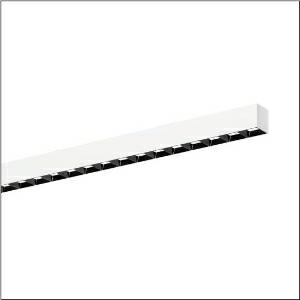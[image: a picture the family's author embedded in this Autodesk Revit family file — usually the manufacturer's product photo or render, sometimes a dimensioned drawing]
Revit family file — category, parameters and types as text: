
# Revit family: silica_21_51mx24tat4w
name_source: partatom
category: Lighting Fixtures
units: mm (PartAtom-declared; Revit-internal decimal feet)

## family parameters
Cut with Voids When Loaded = No
Host = Face
Light Source = No
Part Type = Normal
Room Calculation Point = No
Round Connector Dimension = Use Diameter
Shared = No

## types (1)
- --- (1 x LED, 3280 lm, 32.4 W, 6500K)
    Apparent Load = 32 VA
    CIE Flux Codes = 74 94 99 100 100
    Color Rendering = 80
    Color Temperature = 6500K
    Default Elevation = 1800 mm
    Description = Silica 21, office luminaire, primary light control with darklight reflector, of PMMA, black, light emission: direct distribution, primary light characteristic: asymmetric, installation type: surface-mounted, LED, rated luminous flux: 3.280lm, luminous efficacy: 96lm/W, light colour: 8tw, colour temperature: 2700..6500K, control gear: DALI DT8, with terminal, 3+2-pole, max. 2.5mm², mains connection: 220..240V, AC, 50/60Hz, rated input power: 34.1W, luminaire housing, of aluminium, traffic white (RAL 9016), length: 1.204mm, width: 53mm, height: 53mm, protection rating (complete): IP20, insulation class (complete): insulation class I (protective earthing), certification: CE, permissible operating ambient temperature: 0..+35°C, standard: EN 50419, packaging unit: 1 piece
    Height = 53 mm
    Lamp = 1 x LED
    Lamp Light Flux = 3280 lm
    Lamp Power = 32.4 W
    Lamp count = 1
    Length = 1204 mm
    Luminous efficacy = 101 lm/W
    Manufacturer = Siteco
    ModVariant = No
    Model = 51MX24TAT4W
    Mounting Place = Ceiling
    Mounting Type = Surface mounted
    Number of Poles = 1
    OnlyDefault = Yes
    Power Factor = 1
    Product Name = Silica 21
    Product group = office luminaire | ceiling mounted
    ProductGroupID = 301
    Protection Class = Protection class I
    Protection Degree = IP 20
    RLX_Detail_Level = 1
    RLX_Emergency_Light_Flux = 0 lm
    RLX_Emergency_Type = 0
    RLX_Emergency_Type_DB = No
    RlxData = <blob elided: 38249 chars, md5=07343038>
    Socket = socket
    Standby Power = 0 W
    System Light Flux = 3280 lm
    System Power = 32 W
    Type Comments = individual setting
    Type Image = l_1335873.jpg
    URL = http://relux.com
    VarID = @adj_139511
    Voltage = 0 V
    Weight = 0.00 kg
    Width = 53 mm

## geometry (parser evidence)
native form markers: Blend x4, Sweep x10
no freeform markers — native parametric forms only
